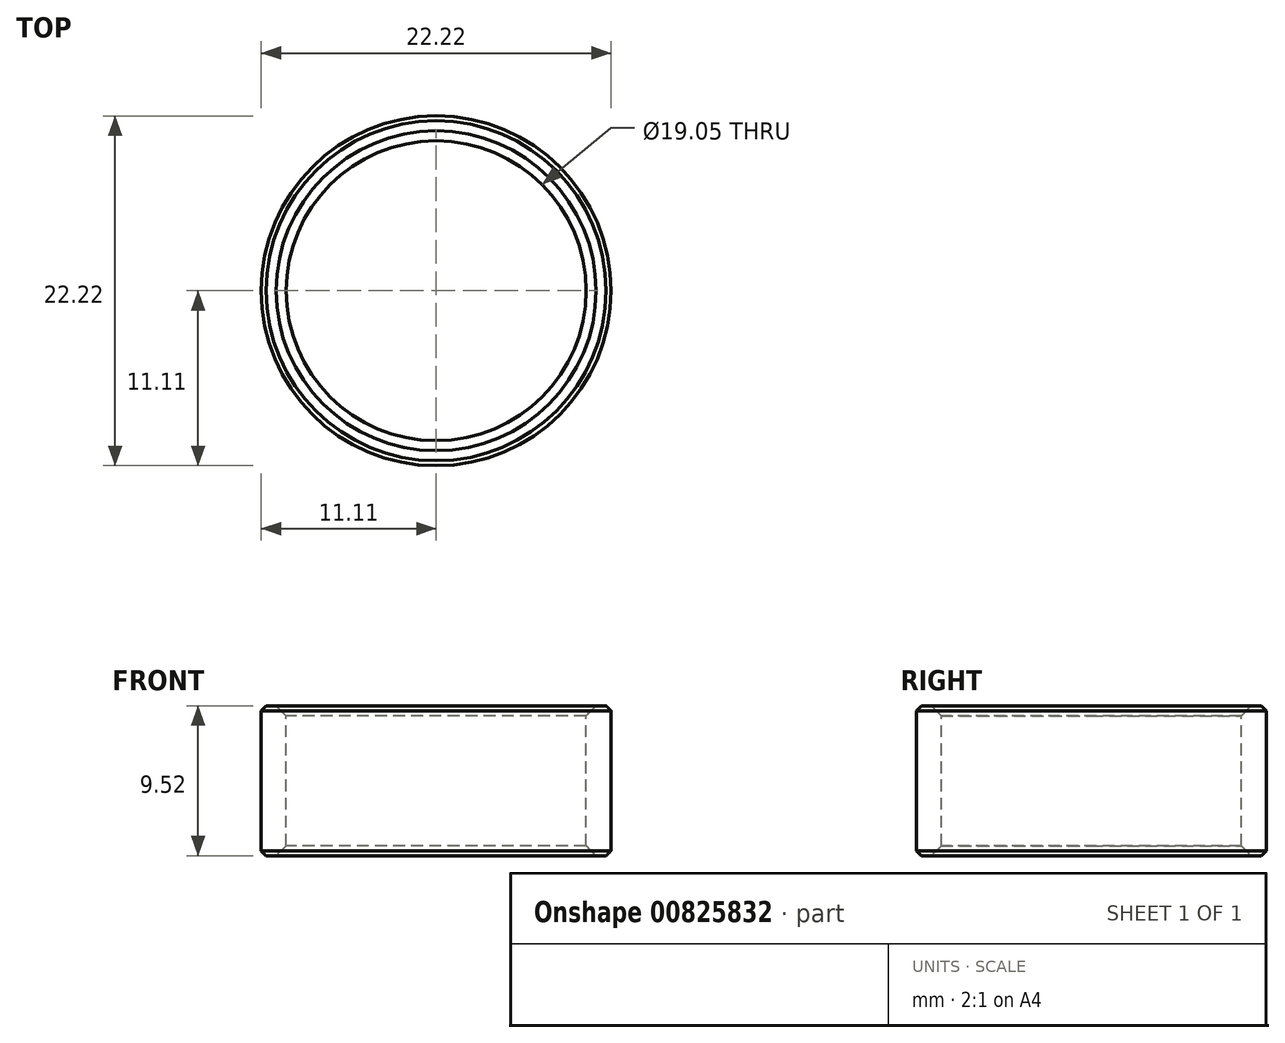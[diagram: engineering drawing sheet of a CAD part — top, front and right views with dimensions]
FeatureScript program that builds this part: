
annotation { "Feature Type Name" : "Feature", "Feature Type Description" : "" }
export const myFeature = defineFeature(function(context is Context, id is Id, definition is map)
    precondition{}
    {
        {
            var Q0;
            Q0=qCreatedBy(makeId("Front.planeOp"),FACE);
            var sketch = newSketch(context, id + "F0", { "sketchPlane" : qUnion([Q0])});
            skLineSegment(sketch, "E0", {"start": v(0, 4.76) * mm, "end": v(0, -4.76) * mm, "construction": true});
            skLineSegment(sketch, "E1.bottom", {"start": v(-9.52, 4.76) * mm, "end": v(-11.11, 4.76) * mm});
            skLineSegment(sketch, "E1.top", {"start": v(-9.52, -4.76) * mm, "end": v(-11.11, -4.76) * mm});
            skLineSegment(sketch, "E1.left", {"start": v(-9.53, 4.76) * mm, "end": v(-9.52, -4.76) * mm});
            skLineSegment(sketch, "E1.right", {"start": v(-11.11, 4.76) * mm, "end": v(-11.11, -4.76) * mm});
            skPoint(sketch, "E2", {"position": v(0, 0) * mm});
            skSolve(sketch);
        }
        {
            var Q0;
            Q0=makeQuery(id+"F0.imprint","IMPRINT",FACE,{"disambiguationData":[TD([[makeQuery(id+"F0.imprint","IMPRINT",EDGE,{"derivedFrom":sQuery(id+"F0.wireOp",EDGE,"E1.bottom")}),1.0]])]});
            var Q1;
            Q1=sQuery(id+"F0.wireOp",EDGE,"E0");
            revolve(context, id + "F1", {"surfaceOperationType" : NewSurfaceOperationType.NEW, "entities" : qUnion([Q0]), "axis" : qUnion([Q1]), "revolveType" : RevolveType.FULL});
        }
        {
            var Q0;
            Q0=makeQuery(id+"F1.opRevolve","SWEPT_EDGE",EDGE,{"disambiguationData":[OSD([sQuery(id+"F0.wireOp",EDGE,"E1.bottom"),sQuery(id+"F0.wireOp",EDGE,"E1.left")])]});
            var Q1;
            Q1=makeQuery(id+"F1.opRevolve","SWEPT_EDGE",EDGE,{"disambiguationData":[OSD([sQuery(id+"F0.wireOp",EDGE,"E1.top"),sQuery(id+"F0.wireOp",EDGE,"E1.left")])]});
            chamfer(context, id + "F2", {"entities" : qUnion([Q0, Q1]), "width" : 0.64 * mm, "tangentPropagation" : true});
        }
        {
            var Q0;
            Q0=makeQuery(id+"F1.opRevolve","SWEPT_EDGE",EDGE,{"disambiguationData":[OSD([sQuery(id+"F0.wireOp",EDGE,"E1.top"),sQuery(id+"F0.wireOp",EDGE,"E1.right")])]});
            var Q1;
            Q1=makeQuery(id+"F1.opRevolve","SWEPT_EDGE",EDGE,{"disambiguationData":[OSD([sQuery(id+"F0.wireOp",EDGE,"E1.bottom"),sQuery(id+"F0.wireOp",EDGE,"E1.right")])]});
            chamfer(context, id + "F3", {"entities" : qUnion([Q0, Q1]), "width" : 0.32 * mm, "tangentPropagation" : true});
        }
    });
